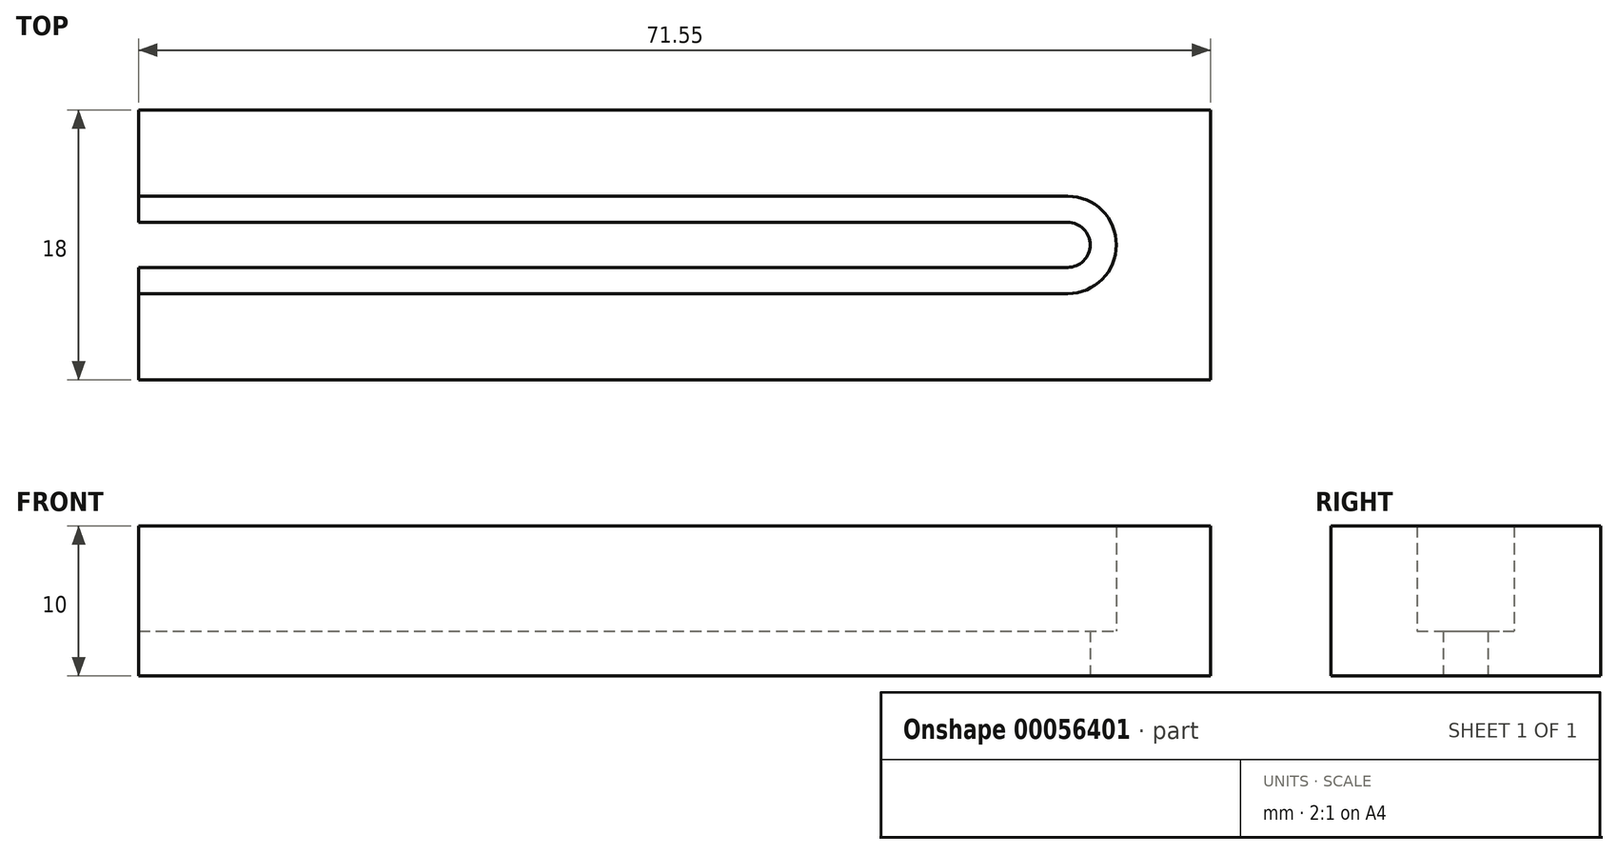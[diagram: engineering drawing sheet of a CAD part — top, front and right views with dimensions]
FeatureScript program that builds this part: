
annotation { "Feature Type Name" : "Feature", "Feature Type Description" : "" }
export const myFeature = defineFeature(function(context is Context, id is Id, definition is map)
    precondition{}
    {
        {
            var Q0;
            Q0=qCreatedBy(makeId("Top.planeOp"),FACE);
            var sketch = newSketch(context, id + "F0", { "sketchPlane" : qUnion([Q0])});
            skLineSegment(sketch, "E0", {"start": v(-33.62, 20.45) * mm, "end": v(28.38, 20.45) * mm});
            skArc(sketch, "E1.0.startCap", {"start": v(-33.62, 17.2) * mm, "mid": v(-36.87, 20.45) * mm, "end": v(-33.62, 23.7) * mm});
            skArc(sketch, "E1.0.endCap", {"start": v(28.38, 23.7) * mm, "mid": v(31.63, 20.45) * mm, "end": v(28.38, 17.2) * mm});
            skLineSegment(sketch, "E1.0.left", {"start": v(-33.62, 23.7) * mm, "end": v(28.38, 23.7) * mm});
            skLineSegment(sketch, "E1.0.right", {"start": v(-33.62, 17.2) * mm, "end": v(28.38, 17.2) * mm});
            skLineSegment(sketch, "E2.bottom", {"start": v(-33.62, 11.45) * mm, "end": v(37.93, 11.45) * mm});
            skLineSegment(sketch, "E2.top", {"start": v(-33.62, 29.45) * mm, "end": v(37.93, 29.45) * mm});
            skLineSegment(sketch, "E2.left", {"start": v(-33.62, 11.45) * mm, "end": v(-33.62, 29.45) * mm});
            skLineSegment(sketch, "E2.right", {"start": v(37.93, 11.45) * mm, "end": v(37.93, 29.45) * mm});
            skArc(sketch, "E3.0.startCap", {"start": v(-33.62, 18.95) * mm, "mid": v(-35.12, 20.45) * mm, "end": v(-33.62, 21.95) * mm});
            skArc(sketch, "E3.0.endCap", {"start": v(28.38, 21.95) * mm, "mid": v(29.88, 20.45) * mm, "end": v(28.38, 18.95) * mm});
            skLineSegment(sketch, "E3.0.left", {"start": v(-33.62, 21.95) * mm, "end": v(28.38, 21.95) * mm});
            skLineSegment(sketch, "E3.0.right", {"start": v(-33.62, 18.95) * mm, "end": v(28.38, 18.95) * mm});
            skSolve(sketch);
        }
        {
            var Q0;
            Q0=makeQuery(id+"F0.imprint","IMPRINT",FACE,{"disambiguationData":[TD([[makeQuery(id+"F0.imprint","IMPRINT",EDGE,{"derivedFrom":sQuery(id+"F0.wireOp",EDGE,"E1.0.endCap")}),1.0]])]});
            extrude(context, id + "F1", {"entities" : qUnion([Q0]), "depth" : 3 * mm});
        }
        {
            var Q0;
            Q0=makeQuery(id+"F0.imprint","IMPRINT",FACE,{"disambiguationData":[TD([[makeQuery(id+"F0.imprint","IMPRINT",EDGE,{"derivedFrom":sQuery(id+"F0.wireOp",EDGE,"E1.0.endCap")}),-1.0]])]});
            var Q1;
            {var subQ0=sQuery(id+"F0.wireOp",EDGE,"E1.0.startCap");Q1=makeQuery(id+"F0.imprint","IMPRINT",FACE,{"disambiguationData":[TD([[makeQuery(id+"F0.imprint","IMPRINT",EDGE,{"derivedFrom":subQ0}),-1.0]])]});}
            extrude(context, id + "F2", {"entities" : qUnion([Q0, Q1]), "operationType" : NewBodyOperationType.ADD, "depth" : 10 * mm});
        }
    });
